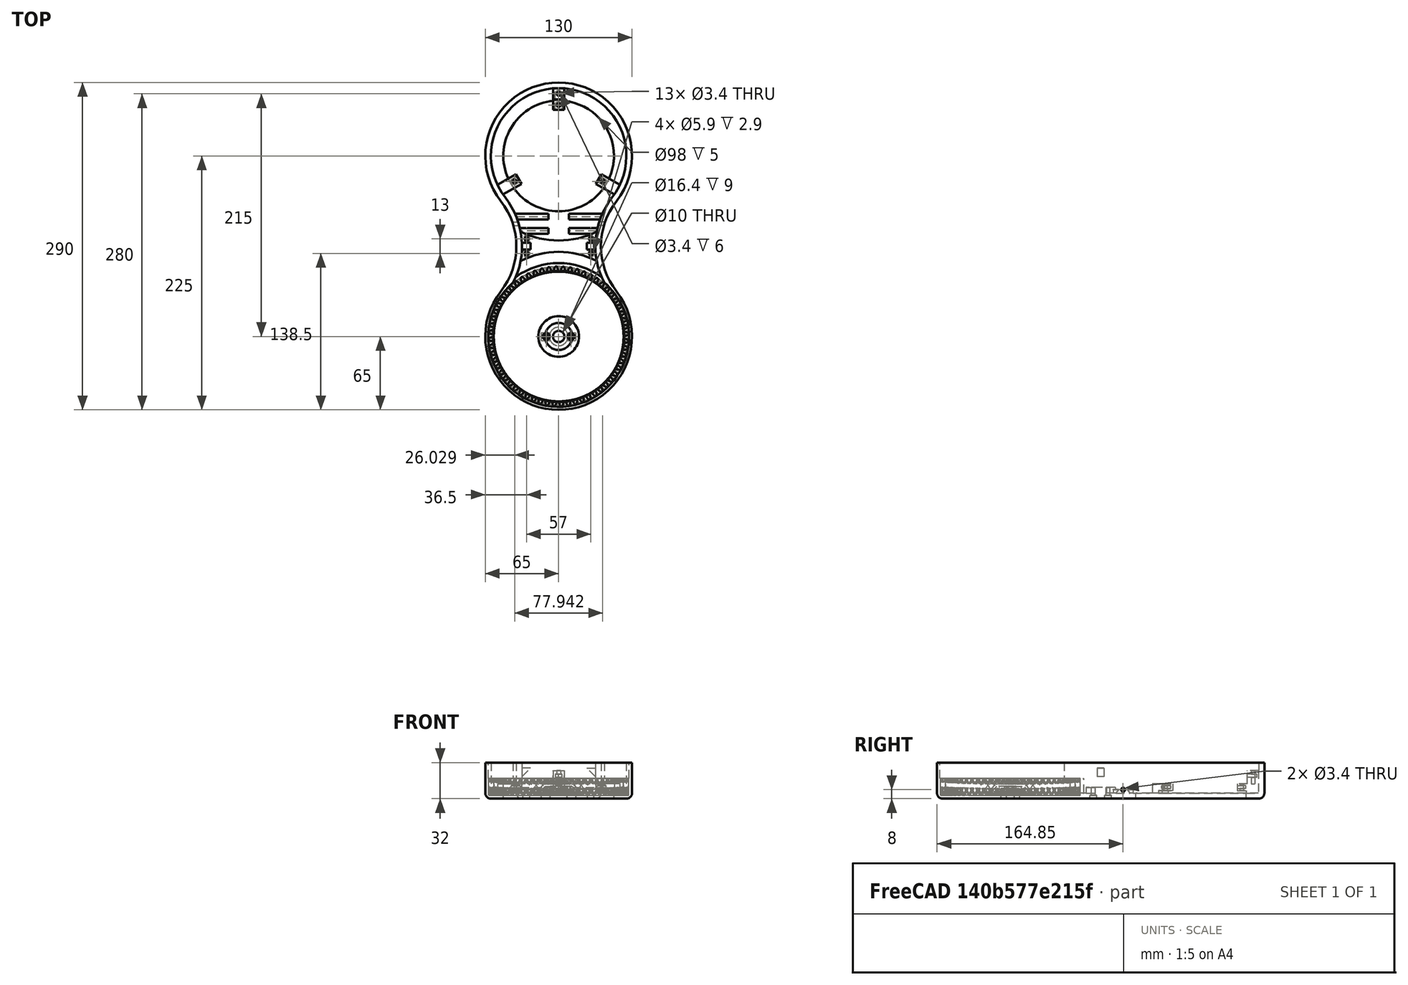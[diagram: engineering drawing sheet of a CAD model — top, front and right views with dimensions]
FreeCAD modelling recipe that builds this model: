
FCSTD DOCUMENT  (FreeCAD 0.16R6703 (Git))
Label: Art2BodyA
License: All rights reserved
LicenseURL: http://en.wikipedia.org/wiki/All_rights_reserved
objects: Part::FeaturePython×25, Part::MultiFuse×11, Part::Cylinder×8, Sketcher::SketchObject×7, Part::Cut×7, PartDesign::Pad×6, Part::Box×4, Part::Prism×1, PartDesign::Revolution×1, Part::Part2DObjectPython×1, Part::Helix×1, Part::Sweep×1, Part::Thickness×1, Part::Fillet×1, App::DocumentObjectGroup×1
note: 82 computed .brp shape members not serialized (recipe doc carries the construction recipe); baked Part::Feature solids carry a one-line shape summary decoded from their .brp

FEATURE [Part::Cylinder] Cylinder  label="M3BoltHead"
  Angle = 360
  Height = 7
  Radius = 2.95
FEATURE [Part::Cylinder] Cylinder001  label="M3BoltBody"
  Angle = 360
  Height = 30
  Placement = pos=(0,0,6) rot=(0,0,1;0rad)
  Radius = 1.7
FEATURE [Part::MultiFuse] Fusion  label="M3Bolt"
  Shapes = -> [Cylinder001,Cylinder]
FEATURE [Sketcher::SketchObject] Sketch003  label="M3NutHousingSketch"
  sketch-geometry (5):
    g0: LineSegment StartX=0 StartY=0 StartZ=0 EndX=1.67432 EndY=2.9 EndZ=0
    g1: LineSegment StartX=1.67432 StartY=2.9 StartZ=0 EndX=21.6743 EndY=2.9 EndZ=0
    g2: LineSegment StartX=21.6743 StartY=2.9 StartZ=0 EndX=21.6743 EndY=-2.9 EndZ=0
    g3: LineSegment StartX=21.6743 StartY=-2.9 StartZ=0 EndX=1.67432 EndY=-2.9 EndZ=0
    g4: LineSegment StartX=1.67432 StartY=-2.9 StartZ=0 EndX=0 EndY=0 EndZ=0
  constraints (14):
    c: Coincident(g-1,g0)
    c: Coincident(g0,g1)
    c: Horizontal(g1)
    c: Coincident(g1,g2)
    c: Vertical(g2)
    c: Coincident(g2,g3)
    c: Horizontal(g3)
    c: Coincident(g3,g4)
    c: Coincident(g4,g0)
    c: Equal(g3,g1)
    c: Equal(g4,g0)
    c: DistanceY(g2) = -5.8
    c: Angle(g-1,g0) = 1.0472
    c: DistanceX(g3) = -20
FEATURE [PartDesign::Pad] Pad002  label="M3NutHousing"
  Length = 2.7
  Length2 = 100
  Sketch = -> Sketch003
  Type = 0
FEATURE [Part::Prism] Prism  label="M3Nut"
  Circumradius = 3.35
  Height = 12
  Polygon = 6
FEATURE [Sketcher::SketchObject] Sketch016
  sketch-geometry (4):
    g0: LineSegment StartX=0 StartY=0 StartZ=0 EndX=0 EndY=18 EndZ=0
    g1: LineSegment StartX=0 StartY=18 StartZ=0 EndX=6 EndY=12 EndZ=0
    g2: LineSegment StartX=6 StartY=12 StartZ=0 EndX=6 EndY=0 EndZ=0
    g3: LineSegment StartX=0 StartY=0 StartZ=0 EndX=6 EndY=0 EndZ=0
  constraints (11):
    c: Coincident(g0,g-1)
    c: Vertical(g0)
    c: Coincident(g1,g0)
    c: Coincident(g2,g1)
    c: PointOnObject(g2,g-1)
    c: Vertical(g2)
    c: Coincident(g3,g-1)
    c: Coincident(g3,g2)
    c: DistanceY(g2) = -12
    c: DistanceX(g3) = 6
    c: Angle(g1,g-1) = 0.785398
FEATURE [PartDesign::Revolution] Revolution003  label="625ZZBearingHousingNoHoles"
  Angle = 360
  Axis = (1,0,0)
  Base = (0,0,0)
  ReferenceAxis = -> Sketch016 [H_Axis]
  Sketch = -> Sketch016
FEATURE [Part::Cylinder] Cylinder1003  label="Bearing625ZZMaster"
  Angle = 360
  Height = 15
  Radius = 8.2
FEATURE [Sketcher::SketchObject] Sketch020
  sketch-geometry (4):
    g0: ArcOfCircle CenterX=0 CenterY=0 CenterZ=0 NormalX=0 NormalY=0 NormalZ=1 Radius=65 StartAngle=2.47872 EndAngle=6.94606
    g1: ArcOfCircle CenterX=102.47 CenterY=80 CenterZ=0 NormalX=0 NormalY=0 NormalZ=1 Radius=65 StartAngle=2.47872 EndAngle=3.80447
    g2: ArcOfCircle CenterX=-102.47 CenterY=80 CenterZ=0 NormalX=0 NormalY=0 NormalZ=1 Radius=65 StartAngle=5.62031 EndAngle=6.94606
    g3: ArcOfCircle CenterX=0 CenterY=160 CenterZ=0 NormalX=0 NormalY=0 NormalZ=1 Radius=65 StartAngle=5.62031 EndAngle=10.0877
  constraints (15):
    c: Coincident(g0,g-1)
    c: Coincident(g1,g0)
    c: Coincident(g2,g0)
    c: Coincident(g3,g1)
    c: Equal(g1,g2)
    c: Equal(g3,g0)
    c: Tangent(g1,g3)
    c: Coincident(g2,g3)
    c: Tangent(g2,g3)
    c: Tangent(g1,g0)
    c: Equal(g0,g2)
    c: Tangent(g0,g2)
    c: DistanceY(g-1,g3) = 160
    c: Radius(g0) = 65
    c: PointOnObject(g3,g-2)
FEATURE [PartDesign::Pad] Pad013
  Length = 32
  Length2 = 100
  Sketch = -> Sketch020
  Type = 0
FEATURE [Part::Part2DObjectPython] InvoluteGear003  # Draft 2D object (typed FeaturePython)
  ExternalGear = true
  HighPrecision = true
  Modules = 2
  NumberOfTeeth = 60
  Placement = pos=(0,0,3) rot=(0,0,1;0rad)
  PressureAngle = 20
FEATURE [Part::Helix] Helix003  label="HelixArt2BodyA"
  Angle = 0
  Height = 15.1
  LocalCoord = 1
  Pitch = 550
  Placement = pos=(0,0,3) rot=(0,0,1;0rad)
  Radius = 1
  Style = 1
FEATURE [Part::Cylinder] Cylinder1009  label="Cylinder016"
  Angle = 360
  Height = 30
  Placement = pos=(0,0,5) rot=(0,0,1;0rad)
  Radius = 62.5
FEATURE [Part::Sweep] Sweep003
  Frenet = true
  Sections = -> [InvoluteGear003]
  Solid = true
  Spine = -> Helix003 [Edge1]
  Transition = 1
FEATURE [Part::Thickness] Thickness001  label="Art2ArmMaster"
  Faces = -> Pad013 [Face6]
  Intersection = false
  Join = 0
  Mode = 0
  SelfIntersection = false
  Value = -5
FEATURE [Part::Cylinder] Cylinder1010  label="Cylinder017"
  Angle = 360
  Height = 13
  Placement = pos=(0,0,5) rot=(0,0,1;0rad)
  Radius = 65
FEATURE [Sketcher::SketchObject] Sketch023
  Placement = pos=(0,0,5) rot=(0,0,1;0rad)
  sketch-geometry (5):
    g0: ArcOfCircle CenterX=0 CenterY=0 CenterZ=0 NormalX=0 NormalY=0 NormalZ=1 Radius=75 StartAngle=1.08528 EndAngle=2.05631
    g1: ArcOfCircle CenterX=0 CenterY=160 CenterZ=0 NormalX=0 NormalY=0 NormalZ=1 Radius=75 StartAngle=4.22687 EndAngle=5.19791
    g2: ArcOfCircle CenterX=115 CenterY=80 CenterZ=0 NormalX=0 NormalY=0 NormalZ=1 Radius=81.1591 StartAngle=2.97238 EndAngle=3.3108
    g3: ArcOfCircle CenterX=-115 CenterY=80 CenterZ=0 NormalX=0 NormalY=0 NormalZ=1 Radius=81.1591 StartAngle=6.11398 EndAngle=6.4524
    g4: LineSegment [constr] StartX=-115 StartY=80 StartZ=0 EndX=115 EndY=80 EndZ=0
  constraints (17):
    c: Coincident(g0,g-1)
    c: PointOnObject(g1,g-2)
    c: Coincident(g2,g1)
    c: Coincident(g2,g0)
    c: Coincident(g3,g1)
    c: Coincident(g3,g0)
    c: Equal(g1,g0)
    c: Equal(g3,g2)
    c: Coincident(g4,g3)
    c: Coincident(g4,g2)
    c: Horizontal(g4)
    c: Radius(g0) = 75
    c: DistanceY(g-1,g1) = 160
    c: DistanceY(g-1,g2) = 80
    c: DistanceX(g4) = 230
    c: DistanceX(g-1,g2) = 115
    c: DistanceX(g0,g0) = 70
FEATURE [PartDesign::Pad] Pad015  label="Art2BodyUnionSupporMaster"
  Length = 5
  Length2 = 100
  Placement = pos=(0,0,5) rot=(0,0,1;0rad)
  Sketch = -> Sketch023
  Type = 0
FEATURE [Part::Cylinder] Cylinder1013  label="Cylinder019"
  Angle = 360
  Height = 10
  Placement = pos=(0,160,0) rot=(0,0,1;0rad)
  Radius = 49
FEATURE [Sketcher::SketchObject] Sketch024
  Placement = pos=(0,0,0) rot=(0.57735,0.57735,0.57735;2.0944rad)
  sketch-geometry (6):
    g0: LineSegment StartX=0 StartY=0 StartZ=0 EndX=0 EndY=8 EndZ=0
    g1: LineSegment StartX=0 StartY=8 StartZ=0 EndX=19 EndY=8 EndZ=0
    g2: LineSegment StartX=19 StartY=8 StartZ=0 EndX=19 EndY=2 EndZ=0
    g3: LineSegment StartX=19 StartY=2 StartZ=0 EndX=11 EndY=2 EndZ=0
    g4: LineSegment StartX=11 StartY=2 StartZ=0 EndX=11 EndY=0 EndZ=0
    g5: LineSegment StartX=11 StartY=0 StartZ=0 EndX=0 EndY=0 EndZ=0
  constraints (17):
    c: Coincident(g-1,g0)
    c: PointOnObject(g0,g-2)
    c: Coincident(g0,g1)
    c: Horizontal(g1)
    c: Coincident(g1,g2)
    c: Vertical(g2)
    c: Coincident(g2,g3)
    c: Horizontal(g3)
    c: Coincident(g3,g4)
    c: Coincident(g4,g5)
    c: Coincident(g5,g0)
    c: Horizontal(g5)
    c: Vertical(g4)
    c: DistanceY(g2) = -6
    c: DistanceX(g3) = -8
    c: DistanceX(g1) = 19
    c: DistanceY(g4) = -2
FEATURE [PartDesign::Pad] Pad016
  Length = 10
  Length2 = 100
  Placement = pos=(0,0,0) rot=(0.57735,0.57735,0.57735;2.0944rad)
  Sketch = -> Sketch024
  Type = 0
FEATURE [Part::FeaturePython] Clone105  label="Clone of M3Bolt030"  # Draft clone (typed FeaturePython)
  Objects = -> [Fusion]
  Placement = pos=(5,15,30) rot=(0,1,0;3.14159rad)
  Scale = (1,1,1)
FEATURE [Part::FeaturePython] Clone106  label="Clone of M3NutHousing008"  # Draft clone (typed FeaturePython)
  Objects = -> [Pad002]
  Placement = pos=(5,11.5,4) rot=(0,0,1;1.5708rad)
  Scale = (1,1,1)
FEATURE [Part::MultiFuse] Fusion045
  Shapes = -> [Clone105,Clone106]
FEATURE [Part::Cut] Cut038
  Base = -> Pad016
  Placement = pos=(5,220,5) rot=(0,0,1;3.14159rad)
  Tool = -> Fusion045
FEATURE [Part::FeaturePython] Array006  # Draft array (typed FeaturePython)
  Angle = 360
  ArrayType = 1
  Axis = (0,0,1)
  Base = -> Cut038
  Center = (0,160,0)
  Fuse = false
  IntervalAxis = (0,0,0)
  IntervalX = (1,0,0)
  IntervalY = (0,1,0)
  IntervalZ = (0,0,0)
  NumberPolar = 3
  NumberX = 2
  NumberY = 2
  NumberZ = 1
FEATURE [Sketcher::SketchObject] Sketch025
  sketch-geometry (3):
    g0: LineSegment StartX=0 StartY=0 StartZ=0 EndX=0 EndY=10 EndZ=0
    g1: LineSegment StartX=0 StartY=10 StartZ=0 EndX=10 EndY=0 EndZ=0
    g2: LineSegment StartX=10 StartY=0 StartZ=0 EndX=0 EndY=0 EndZ=0
  constraints (8):
    c: Coincident(g-1,g0)
    c: PointOnObject(g0,g-2)
    c: Coincident(g0,g1)
    c: PointOnObject(g1,g-1)
    c: Coincident(g1,g2)
    c: Coincident(g2,g0)
    c: DistanceY(g0) = 10
    c: Angle(g1,g2) = 0.785398
FEATURE [PartDesign::Pad] Pad017  label="Art2CoverArmSupportMaster"
  Length = 6
  Length2 = 100
  Sketch = -> Sketch025
  Type = 0
FEATURE [Part::FeaturePython] Clone107  label="Clone of Art2CoverArmSupportMaster"  # Draft clone (typed FeaturePython)
  Objects = -> [Pad017]
  Placement = pos=(-35,77,27) rot=(-1,0,0;1.5708rad)
  Scale = (1,1,1)
FEATURE [Part::FeaturePython] Clone108  label="Clone of Art2CoverArmSupportMaster001"  # Draft clone (typed FeaturePython)
  Objects = -> [Pad017]
  Placement = pos=(35,83,27) rot=(0,-0.707107,0.707107;3.14159rad)
  Scale = (1,1,1)
FEATURE [Part::FeaturePython] Clone109  label="Clone of Art2BodyUnionSupporMaster"  # Draft clone (typed FeaturePython)
  Objects = -> [Pad015]
  Placement = pos=(0,0,5) rot=(0,0,1;0rad)
  Scale = (1,1,1)
FEATURE [Sketcher::SketchObject] Sketch026
  Placement = pos=(0,0,0) rot=(0.57735,0.57735,0.57735;2.0944rad)
  sketch-geometry (8):
    g0: LineSegment StartX=0 StartY=0 StartZ=0 EndX=0 EndY=5 EndZ=0
    g1: LineSegment StartX=0 StartY=5 StartZ=0 EndX=5 EndY=5 EndZ=0
    g2: LineSegment StartX=5 StartY=5 StartZ=0 EndX=2.45 EndY=1.96103 EndZ=0
    g3: LineSegment StartX=2.45 StartY=1.96103 StartZ=0 EndX=15.25 EndY=1.96103 EndZ=0
    g4: LineSegment StartX=15.25 StartY=1.96103 StartZ=0 EndX=12.7 EndY=5 EndZ=0
    g5: LineSegment StartX=12.7 StartY=5 StartZ=0 EndX=17.7 EndY=5 EndZ=0
    g6: LineSegment StartX=17.7 StartY=5 StartZ=0 EndX=17.7 EndY=0 EndZ=0
    g7: LineSegment StartX=17.7 StartY=0 StartZ=0 EndX=0 EndY=0 EndZ=0
  constraints (23):
    c: Coincident(g-1,g0)
    c: PointOnObject(g0,g-2)
    c: Coincident(g0,g1)
    c: Horizontal(g1)
    c: Coincident(g1,g2)
    c: Coincident(g2,g3)
    c: Horizontal(g3)
    c: Coincident(g3,g4)
    c: Coincident(g4,g5)
    c: Horizontal(g5)
    c: Coincident(g5,g6)
    c: PointOnObject(g6,g-1)
    c: Coincident(g6,g7)
    c: Coincident(g7,g0)
    c: Vertical(g6)
    c: Equal(g5,g1)
    c: Equal(g2,g4)
    c: Angle(g3,g2) = 0.872665
    c: DistanceX(g1) = 5
    c: Angle(g4,g3) = 0.872665
    c: DistanceX(g3) = 12.8
    c: DistanceX(g1,g4) = 7.7
    c: DistanceY(g-1,g0) = 5
FEATURE [PartDesign::Pad] Pad018  label="Art2BodyAMilanoMaster"
  Length = 30
  Length2 = 100
  Placement = pos=(0,0,0) rot=(0.57735,0.57735,0.57735;2.0944rad)
  Sketch = -> Sketch026
  Type = 0
FEATURE [Part::Box] Box248  label="Cube012"
  Height = 10
  Length = 10
  Placement = pos=(33.8236,89.3815,3) rot=(0,0,-1;0.261799rad)
  Width = 20
FEATURE [Part::FeaturePython] Clone110  label="Clone of Art2BodyAMilanoMaster"  # Draft clone (typed FeaturePython)
  Objects = -> [Pad018]
  Placement = pos=(-39,91,3) rot=(0.57735,0.57735,0.57735;2.0944rad)
  Scale = (1,1,1)
FEATURE [Part::FeaturePython] Clone111  label="Clone of Art2BodyAMilanoMaster001"  # Draft clone (typed FeaturePython)
  Objects = -> [Pad018]
  Placement = pos=(39,108.7,3) rot=(0.57735,-0.57735,-0.57735;2.0944rad)
  Scale = (1,1,1)
FEATURE [Part::Box] Box249  label="Cube013"
  Height = 10
  Length = 10
  Placement = pos=(-43.4829,86.7933,3) rot=(0,0,1;0.261799rad)
  Width = 20
FEATURE [Part::MultiFuse] Fusion047
  Shapes = -> [Clone110,Clone111]
FEATURE [Part::MultiFuse] Fusion048
  Shapes = -> [Box249,Box248]
FEATURE [Part::FeaturePython] Clone112  label="Clone of M3Bolt031"  # Draft clone (typed FeaturePython)
  Objects = -> [Fusion]
  Placement = pos=(28.5,86.5,-4.1) rot=(0,0,1;3.14159rad)
  Scale = (1,1,1)
FEATURE [Part::FeaturePython] Clone113  label="Clone of M3Bolt032"  # Draft clone (typed FeaturePython)
  Objects = -> [Fusion]
  Placement = pos=(-28.5,86.5,-4.1) rot=(0,0,1;3.14159rad)
  Scale = (1,1,1)
FEATURE [Part::FeaturePython] Clone114  label="Clone of M3Bolt033"  # Draft clone (typed FeaturePython)
  Objects = -> [Fusion]
  Placement = pos=(28.5,73.5,-4.1) rot=(0,0,1;3.14159rad)
  Scale = (1,1,1)
FEATURE [Part::FeaturePython] Clone115  label="Clone of M3Bolt034"  # Draft clone (typed FeaturePython)
  Objects = -> [Fusion]
  Placement = pos=(-28.5,73.5,-4.1) rot=(0,0,1;3.14159rad)
  Scale = (1,1,1)
FEATURE [Part::FeaturePython] Clone116  label="Clone of M3Bolt035"  # Draft clone (typed FeaturePython)
  Objects = -> [Fusion]
  Placement = pos=(-58,99.85,8) rot=(0,1,0;1.5708rad)
  Scale = (1,1,1)
FEATURE [Part::FeaturePython] Clone117  label="Clone of M3Bolt036"  # Draft clone (typed FeaturePython)
  Objects = -> [Fusion]
  Placement = pos=(64,99.85,8) rot=(0,-1,0;1.5708rad)
  Scale = (1,1,1)
FEATURE [Part::MultiFuse] Fusion050
  Shapes = -> [Clone117,Clone112,Clone116,Clone115,Clone113,Clone114]
FEATURE [Part::Box] Box250  label="Cube014"
  Height = 20
  Length = 10
  Width = 10
FEATURE [Part::FeaturePython] Clone118  label="Clone of M3Bolt037"  # Draft clone (typed FeaturePython)
  Objects = -> [Fusion]
  Placement = pos=(5,5,40) rot=(1,0,0;3.14159rad)
  Scale = (1,1,1)
FEATURE [Part::FeaturePython] Clone119  label="Clone of M3NutHousing009"  # Draft clone (typed FeaturePython)
  Objects = -> [Pad002]
  Placement = pos=(1.5,5,14) rot=(0,0,1;0rad)
  Scale = (1,1,1)
FEATURE [Part::MultiFuse] Fusion051
  Shapes = -> [Clone118,Clone119]
FEATURE [Part::Cut] Cut040  label="Art2BodyCoverFix"
  Base = -> Box250
  Tool = -> Fusion051
FEATURE [Part::FeaturePython] Clone136  label="Clone of Bearing625ZZMaster"  # Draft clone (typed FeaturePython)
  Objects = -> [Cylinder1003]
  Placement = pos=(0,0,-6) rot=(0,0,1;0rad)
  Scale = (1,1,1)
FEATURE [Part::Cylinder] Cylinder1015  label="Cylinder021"
  Angle = 360
  Height = 10
  Placement = pos=(0,0,4) rot=(0,0,1;0rad)
  Radius = 5
FEATURE [Part::Box] Box251  label="Cube015"
  Height = 4
  Length = 30.6
  Placement = pos=(-15.3,-3.5,0) rot=(0,0,1;0rad)
  Width = 7
FEATURE [Part::FeaturePython] Clone137  label="Clone of M3Bolt039"  # Draft clone (typed FeaturePython)
  Objects = -> [Fusion]
  Placement = pos=(11,0,-4) rot=(0,0,1;0rad)
  Scale = (1,1,1)
FEATURE [Part::FeaturePython] Clone138  label="Clone of M3Bolt040"  # Draft clone (typed FeaturePython)
  Objects = -> [Fusion]
  Placement = pos=(-11,0,-4) rot=(0,0,1;0rad)
  Scale = (1,1,1)
FEATURE [Part::FeaturePython] Clone139  label="Clone of M3Nut005"  # Draft clone (typed FeaturePython)
  Objects = -> [Prism]
  Placement = pos=(11,0,7) rot=(0,0,1;0.523599rad)
  Scale = (1,1,1)
FEATURE [Part::FeaturePython] Clone140  label="Clone of M3Nut006"  # Draft clone (typed FeaturePython)
  Objects = -> [Prism]
  Placement = pos=(-11,0,7) rot=(0,0,1;0.523599rad)
  Scale = (1,1,1)
FEATURE [Part::MultiFuse] Fusion062  label="Bearing625zzHoles"
  Shapes = -> [Clone140,Clone139,Box251,Clone137,Clone138,Cylinder1015,Clone136]
FEATURE [Part::FeaturePython] Clone146  label="Clone of Art2BodyCoverFix"  # Draft clone (typed FeaturePython)
  Objects = -> [Cut040]
  Placement = pos=(-5,220,5) rot=(0,0,-1;1.5708rad)
  Scale = (1,1,1)
FEATURE [Part::FeaturePython] Clone373  label="Clone of 625ZZBearingHousingNoHoles005"  # Draft clone (typed FeaturePython)
  Objects = -> [Revolution003]
  Placement = pos=(0,0,5) rot=(0,-1,0;1.5708rad)
  Scale = (1,1,1)
FEATURE [Part::FeaturePython] Clone375  label="Clone of Bearing625zzHoles006"  # Draft clone (typed FeaturePython)
  Objects = -> [Fusion062]
  Scale = (1,1,1)
FEATURE [Part::Cylinder] Cylinder1048  label="Cylinder1090"
  Angle = 360
  Height = 2
  Placement = pos=(0,0,3) rot=(0,0,1;0rad)
  Radius = 18
FEATURE [Part::MultiFuse] Fusion141
  Shapes = -> [Cylinder1013,Clone375]
FEATURE [Part::Cut] Cut039
  Base = -> Fusion047
  Tool = -> Fusion048
FEATURE [Part::FeaturePython] Clone441  label="Clone of Art2ArmMaster"  # Draft clone (typed FeaturePython)
  Objects = -> [Thickness001]
  Scale = (1,1,1)
FEATURE [Part::Cut] Cut144  label="Cut177"
  Base = -> Clone441
  Tool = -> Cylinder1009
FEATURE [Part::MultiFuse] Fusion165
  Shapes = -> [Cut144,Cylinder1010]
FEATURE [Part::Cut] Cut145  label="Cut178"
  Base = -> Fusion165
  Tool = -> Sweep003
FEATURE [Part::MultiFuse] Fusion166
  Shapes = -> [Clone373,Cylinder1048,Cut145]
FEATURE [Part::Cut] Cut146  label="Cut179"
  Base = -> Fusion166
  Tool = -> Fusion141
FEATURE [Part::MultiFuse] Fusion167
  Shapes = -> [Cut146,Clone109,Cut039,Array006,Clone146,Clone107,Clone108]
FEATURE [Part::Cut] Cut147  label="Cut180"
  Base = -> Fusion167
  Tool = -> Fusion050
FEATURE [Part::Fillet] Fillet010  label="Art2BodyAMaster"
  Base = -> Cut147
  Edges = 4 edges r=5: [Edge184,Edge185,Edge186,Edge187]
FEATURE [App::DocumentObjectGroup] Group  label="Master"
  Group = -> [Fusion,Pad002,Prism,Revolution003,Cylinder1003,Helix003,Thickness001,Pad015,Pad017,Pad018,Cut040,Fusion062]
